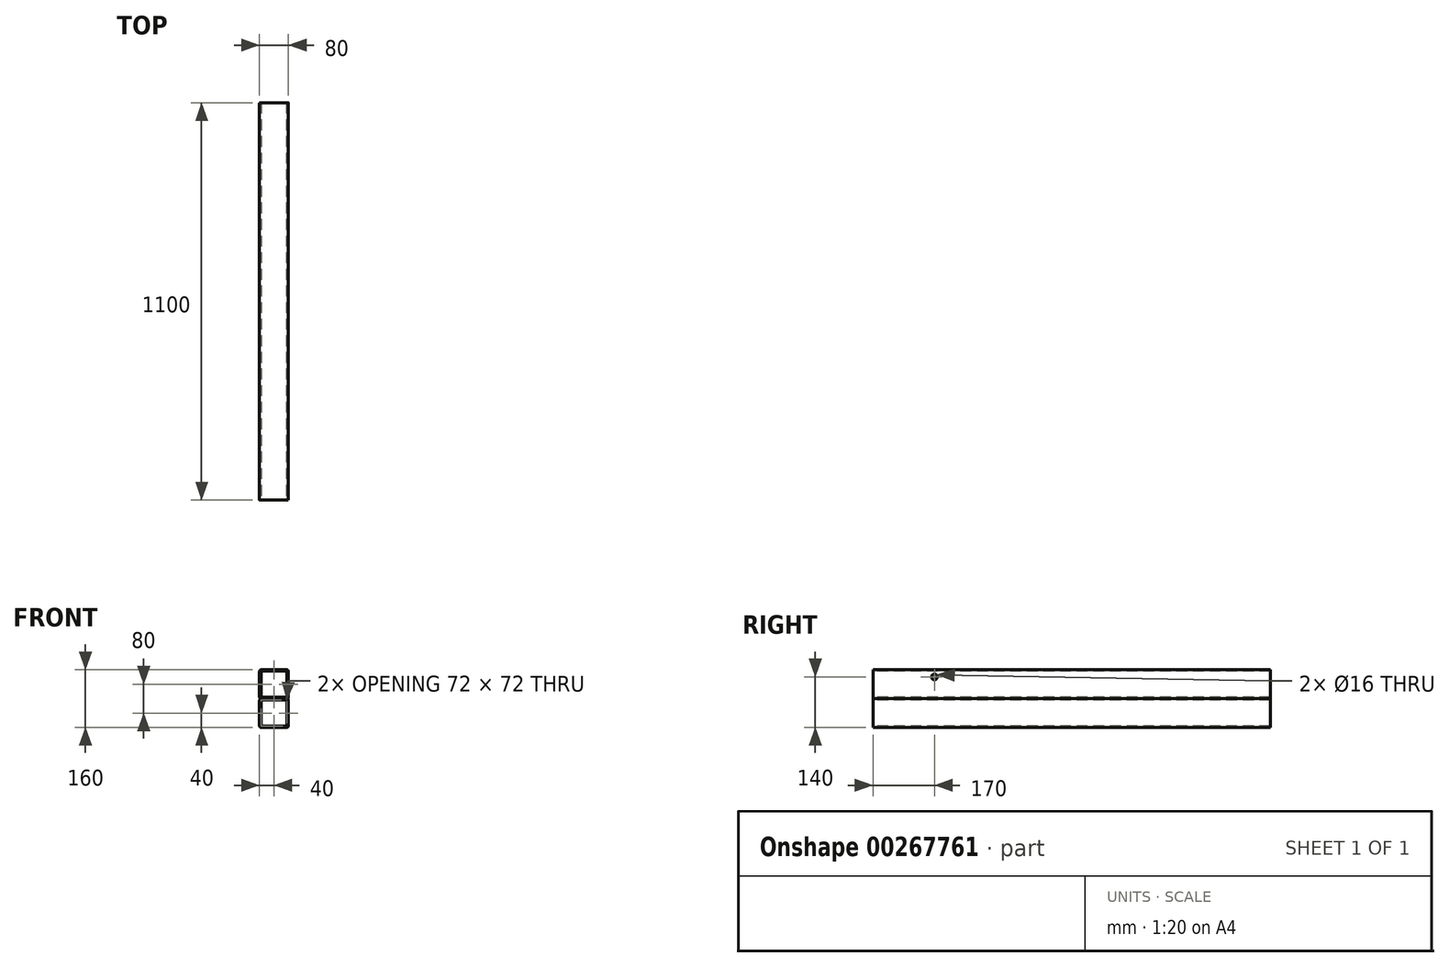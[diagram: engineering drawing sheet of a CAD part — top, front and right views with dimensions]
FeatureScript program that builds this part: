
annotation { "Feature Type Name" : "Feature", "Feature Type Description" : "" }
export const myFeature = defineFeature(function(context is Context, id is Id, definition is map)
    precondition{}
    {
        {
            var Q0;
            Q0=qCreatedBy(makeId("Front.planeOp"),FACE);
            var sketch = newSketch(context, id + "F0", { "sketchPlane" : qUnion([Q0])});
            skLineSegment(sketch, "E0.bottom", {"start": v(35, 40) * mm, "end": v(-35, 40) * mm});
            skLineSegment(sketch, "E0.top", {"start": v(35, -40) * mm, "end": v(-35, -40) * mm});
            skLineSegment(sketch, "E0.left", {"start": v(40, 35) * mm, "end": v(40, -35) * mm});
            skLineSegment(sketch, "E0.right", {"start": v(-40, 35) * mm, "end": v(-40, -35) * mm});
            skPoint(sketch, "E0.middle", {"position": v(0, 0) * mm});
            skPoint(sketch, "E1.visualSharp", {"position": v(-40, 40) * mm});
            skArc(sketch, "E1.filletArc", {"start": v(-35, 40) * mm, "mid": v(-38.54, 38.54) * mm, "end": v(-40, 35) * mm});
            skPoint(sketch, "E2.visualSharp", {"position": v(40, 40) * mm});
            skArc(sketch, "E2.filletArc", {"start": v(40, 35) * mm, "mid": v(38.54, 38.54) * mm, "end": v(35, 40) * mm});
            skPoint(sketch, "E3.visualSharp", {"position": v(40, -40) * mm});
            skArc(sketch, "E3.filletArc", {"start": v(35, -40) * mm, "mid": v(38.54, -38.54) * mm, "end": v(40, -35) * mm});
            skPoint(sketch, "E4.visualSharp", {"position": v(-40, -40) * mm});
            skArc(sketch, "E4.filletArc", {"start": v(-40, -35) * mm, "mid": v(-38.54, -38.54) * mm, "end": v(-35, -40) * mm});
            skArc(sketch, "E5.0", {"start": v(-35, 36) * mm, "mid": v(-35.7, 35.7) * mm, "end": v(-36, 35) * mm});
            skLineSegment(sketch, "E5.1", {"start": v(35, 36) * mm, "end": v(-35, 36) * mm});
            skLineSegment(sketch, "E5.2", {"start": v(-36, 35) * mm, "end": v(-36, -35) * mm});
            skArc(sketch, "E5.3", {"start": v(36, 35) * mm, "mid": v(35.7, 35.7) * mm, "end": v(35, 36) * mm});
            skArc(sketch, "E5.4", {"start": v(-36, -35) * mm, "mid": v(-35.7, -35.7) * mm, "end": v(-35, -36) * mm});
            skLineSegment(sketch, "E5.5", {"start": v(35, -36) * mm, "end": v(-35, -36) * mm});
            skArc(sketch, "E5.6", {"start": v(35, -36) * mm, "mid": v(35.7, -35.7) * mm, "end": v(36, -35) * mm});
            skLineSegment(sketch, "E5.7", {"start": v(36, 35) * mm, "end": v(36, -35) * mm});
            skLineSegment(sketch, "E6.top", {"start": v(35, -120) * mm, "end": v(-35, -120) * mm});
            skLineSegment(sketch, "E6.left", {"start": v(40, -45) * mm, "end": v(40, -115) * mm});
            skLineSegment(sketch, "E6.right", {"start": v(-40, -45) * mm, "end": v(-40, -115) * mm});
            skPoint(sketch, "E6.middle", {"position": v(0, -80) * mm});
            skArc(sketch, "E7.filletArc", {"start": v(-35, -40) * mm, "mid": v(-38.54, -41.46) * mm, "end": v(-40, -45) * mm});
            skArc(sketch, "E8.filletArc", {"start": v(40, -45) * mm, "mid": v(38.54, -41.46) * mm, "end": v(35, -40) * mm});
            skPoint(sketch, "E9.visualSharp", {"position": v(40, -120) * mm});
            skArc(sketch, "E9.filletArc", {"start": v(35, -120) * mm, "mid": v(38.54, -118.54) * mm, "end": v(40, -115) * mm});
            skPoint(sketch, "E10.visualSharp", {"position": v(-40, -120) * mm});
            skArc(sketch, "E10.filletArc", {"start": v(-40, -115) * mm, "mid": v(-38.54, -118.54) * mm, "end": v(-35, -120) * mm});
            skArc(sketch, "E11.0", {"start": v(-35, -44) * mm, "mid": v(-35.7, -44.3) * mm, "end": v(-36, -45) * mm});
            skLineSegment(sketch, "E11.1", {"start": v(35, -44) * mm, "end": v(-35, -44) * mm});
            skLineSegment(sketch, "E11.2", {"start": v(-36, -45) * mm, "end": v(-36, -115) * mm});
            skArc(sketch, "E11.3", {"start": v(36, -45) * mm, "mid": v(35.7, -44.3) * mm, "end": v(35, -44) * mm});
            skArc(sketch, "E11.4", {"start": v(-36, -115) * mm, "mid": v(-35.7, -115.7) * mm, "end": v(-35, -116) * mm});
            skLineSegment(sketch, "E11.5", {"start": v(35, -116) * mm, "end": v(-35, -116) * mm});
            skArc(sketch, "E11.6", {"start": v(35, -116) * mm, "mid": v(35.7, -115.7) * mm, "end": v(36, -115) * mm});
            skLineSegment(sketch, "E11.7", {"start": v(36, -45) * mm, "end": v(36, -115) * mm});
            skSolve(sketch);
        }
        {
            var Q0;
            Q0=makeQuery(id+"F0.imprint","IMPRINT",FACE,{"disambiguationData":[TD([[makeQuery(id+"F0.imprint","IMPRINT",EDGE,{"derivedFrom":sQuery(id+"F0.wireOp",EDGE,"E0.bottom")}),1.0]])]});
            var Q1;
            Q1=makeQuery(id+"F0.imprint","IMPRINT",FACE,{"disambiguationData":[TD([[makeQuery(id+"F0.imprint","IMPRINT",EDGE,{"derivedFrom":sQuery(id+"F0.wireOp",EDGE,"E0.top")}),1.0]])]});
            extrude(context, id + "F1", {"entities" : qUnion([Q0, Q1]), "oppositeDirection" : true, "depth" : 1100 * mm});
        }
        {
            var Q0;
            Q0=makeQuery(id+"F1.opExtrude","SWEPT_FACE",FACE,{"disambiguationData":[OSD([sQuery(id+"F0.wireOp",EDGE,"E0.left")])]});
            var sketch = newSketch(context, id + "F2", { "sketchPlane" : qUnion([Q0])});
            skCircle(sketch, "E12", {"center": v(170, 20) * mm, "radius": 8 * mm});
            skSolve(sketch);
        }
        {
            var Q0;
            Q0=makeQuery(id+"F2.imprint","IMPRINT",FACE,{"disambiguationData":[TD([[makeQuery(id+"F2.imprint","IMPRINT",EDGE,{"derivedFrom":sQuery(id+"F2.wireOp",EDGE,"E12")}),1.0]])]});
            extrude(context, id + "F3", {"entities" : qUnion([Q0]), "operationType" : NewBodyOperationType.REMOVE, "endBound" : BoundingType.THROUGH_ALL, "oppositeDirection" : true, "depth" : 25 * mm});
        }
    });
